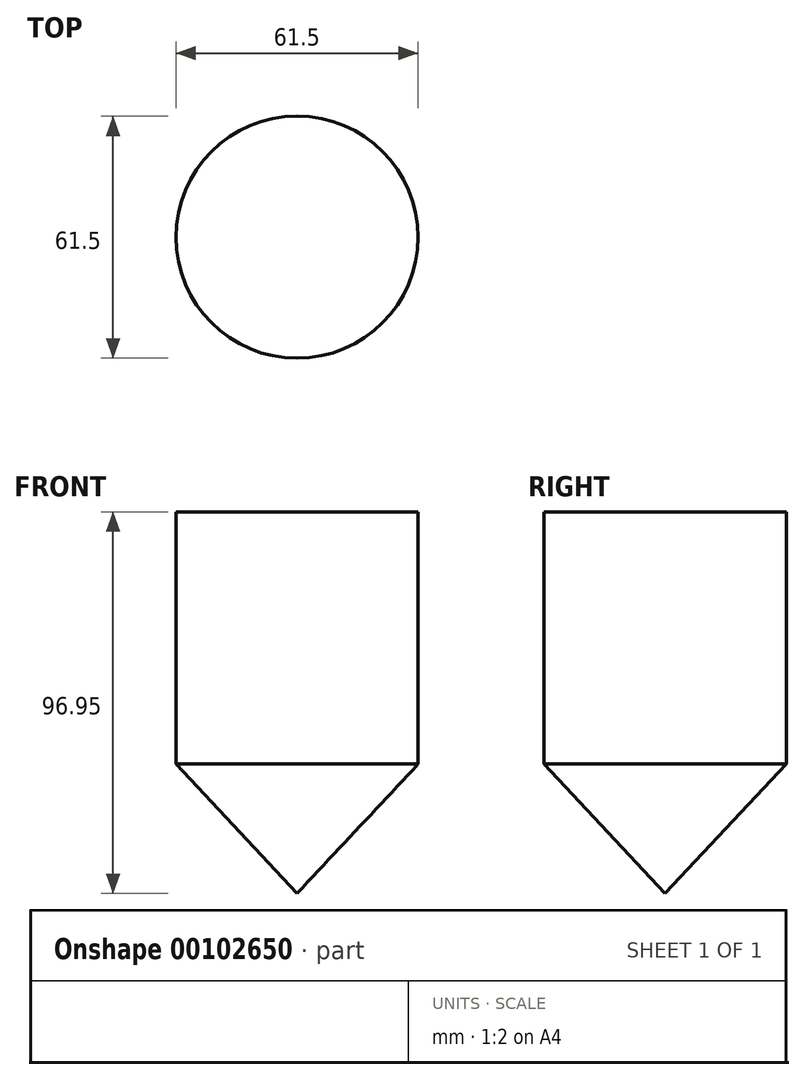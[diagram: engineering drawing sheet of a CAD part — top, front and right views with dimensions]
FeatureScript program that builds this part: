
annotation { "Feature Type Name" : "Feature", "Feature Type Description" : "" }
export const myFeature = defineFeature(function(context is Context, id is Id, definition is map)
    precondition{}
    {
        {
            var Q0;
            Q0=qCreatedBy(makeId("Front.planeOp"),FACE);
            var sketch = newSketch(context, id + "F0", { "sketchPlane" : qUnion([Q0])});
            skLineSegment(sketch, "E0", {"start": v(0, 40.14) * mm, "end": v(30.75, 40.14) * mm});
            skLineSegment(sketch, "E1", {"start": v(30.75, 40.14) * mm, "end": v(30.75, -23.98) * mm});
            skLineSegment(sketch, "E2", {"start": v(30.75, -23.98) * mm, "end": v(0, -56.81) * mm});
            skLineSegment(sketch, "E3", {"start": v(0, -56.81) * mm, "end": v(0, 40.14) * mm});
            skLineSegment(sketch, "E4", {"start": v(0, 60.72) * mm, "end": v(0, -72.71) * mm});
            skSolve(sketch);
        }
        {
            var Q0;
            {var subQ0=sQuery(id+"F0.wireOp",EDGE,"E0");Q0=makeQuery(id+"F0.imprint","IMPRINT",FACE,{"disambiguationData":[TD([[makeQuery(id+"F0.imprint","IMPRINT",EDGE,{"derivedFrom":subQ0}),-1.0]])]});}
            var Q1;
            Q1=sQuery(id+"F0.wireOp",EDGE,"E4");
            revolve(context, id + "F1", {"entities" : qUnion([Q0]), "axis" : qUnion([Q1]), "revolveType" : RevolveType.FULL});
        }
    });
